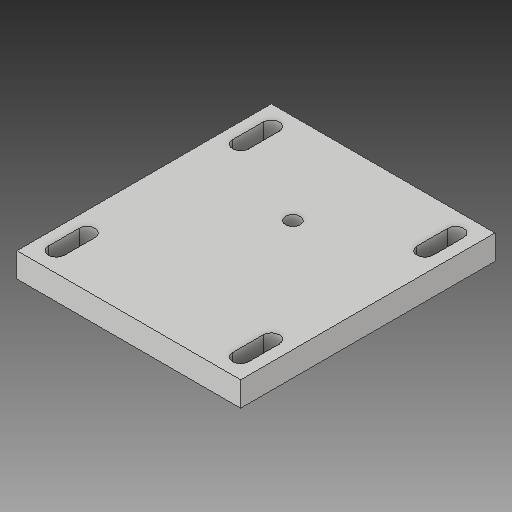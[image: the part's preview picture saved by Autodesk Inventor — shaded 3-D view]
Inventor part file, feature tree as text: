
AUTODESK INVENTOR PART (.ipt)
format: ipt  version: 2019 (Build 230136000, 136)  size: 151,040 bytes
history: native  units: mm
features: extrude x1, sketch x1
ambient origin geometry x8: Origin, YZ Plane, XZ Plane, XY Plane, X Axis, Y Axis, Z Axis, Center Point
bodies: Body1 (feature_tree)
feature tree (2):
  extrude  "Extrusion2"  TaperAngle=180.0deg  [1 undecoded]
  sketch  "Sketch2"  dims[d25=6.5mm d26=180.0deg d27=3.25mm d28=12.5mm d29=90.0deg d30=12.5mm d31=90.0deg d32=3.25mm d33=6.5mm d34=180.0deg d35=3.25mm d36=12.5mm d37=90.0deg d38=12.5mm d39=90.0deg d40=3.25mm d41=25.0mm d42=25.0mm d43=6.5mm d44=180.0deg d45=3.25mm d46=12.5mm d47=90.0deg d48=12.5mm d49=90.0deg d50=3.25mm d51=6.5mm d52=180.0deg d53=3.25mm d54=12.5mm d55=90.0deg d56=12.5mm d57=90.0deg d58=3.25mm d59=75.0mm d60=0.0mm d61=75.0mm d62=0.0mm d63=75.0mm d64=75.0mm d65=8.0mm d66=8.0mm d67=8.0mm d68=8.0mm d71=6.0mm d74=10.0mm d75=0.0mm d76=16.25mm d77=37.5mm]
note: 1 required parameter value undecoded (feature->parameter linkage not recoverable at this tier; creation-order binding heuristic only, values carry confidence <= 0.55)
